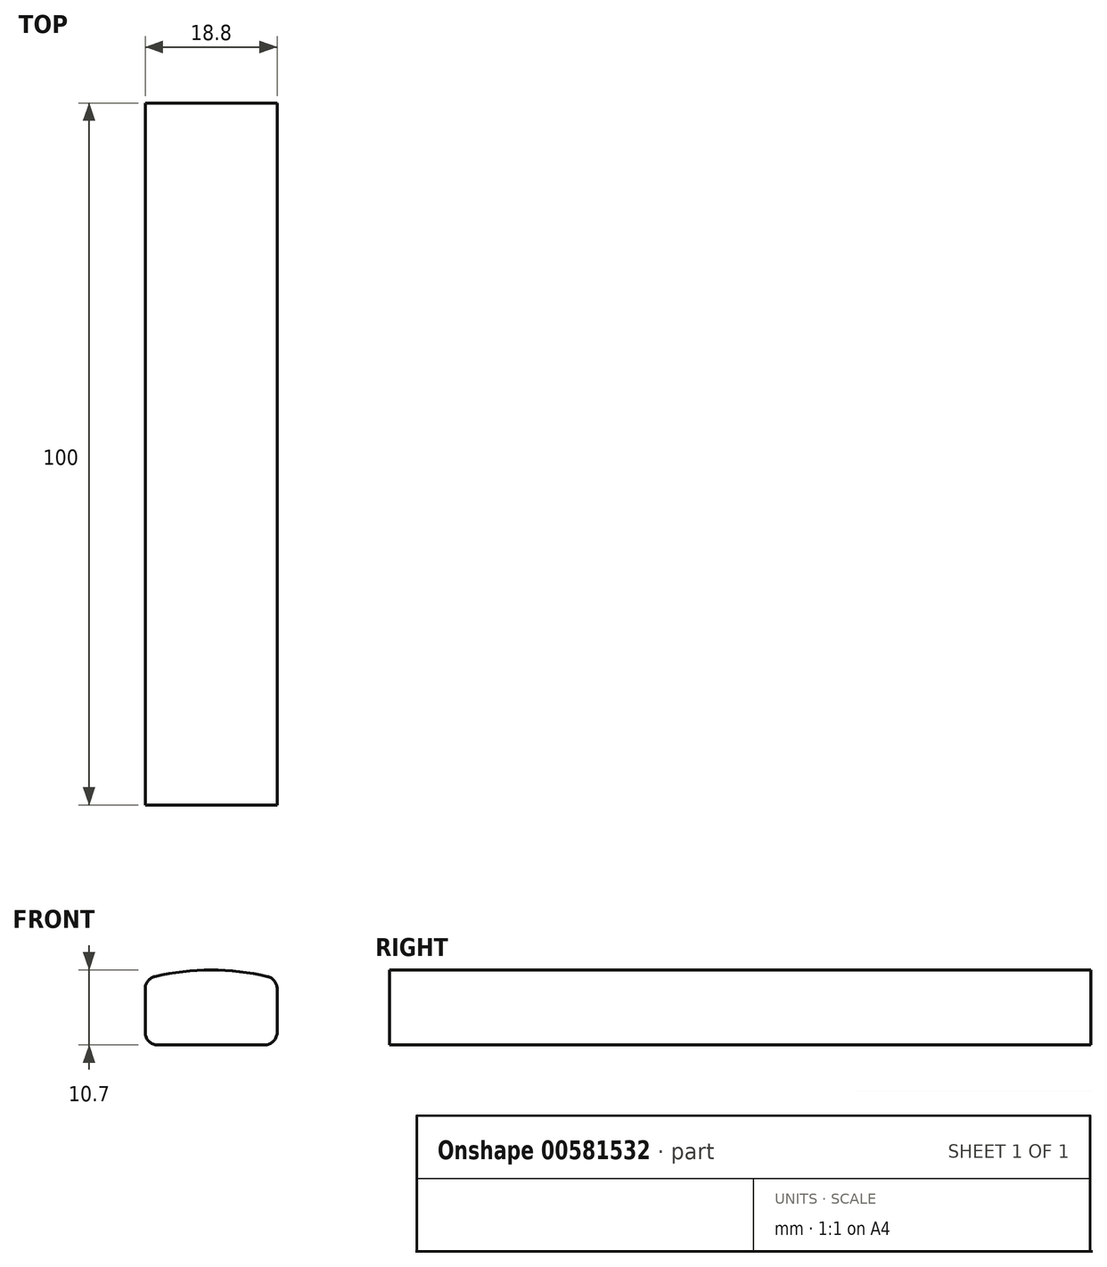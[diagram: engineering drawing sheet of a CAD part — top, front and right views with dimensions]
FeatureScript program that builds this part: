
annotation { "Feature Type Name" : "Feature", "Feature Type Description" : "" }
export const myFeature = defineFeature(function(context is Context, id is Id, definition is map)
    precondition{}
    {
        {
            var Q0;
            Q0=qCreatedBy(makeId("Front.planeOp"),FACE);
            var sketch = newSketch(context, id + "F0", { "sketchPlane" : qUnion([Q0])});
            skLineSegment(sketch, "E0.top", {"start": v(-7.6, -4.7) * mm, "end": v(7.6, -4.7) * mm});
            skLineSegment(sketch, "E0.left", {"start": v(-9.4, 3.3) * mm, "end": v(-9.4, -2.9) * mm});
            skLineSegment(sketch, "E0.right", {"start": v(9.4, 3.3) * mm, "end": v(9.4, -2.9) * mm});
            skPoint(sketch, "E0.middle", {"position": v(0, 0) * mm});
            skArc(sketch, "E1", {"start": v(-8.02, 5.06) * mm, "mid": v(0, 6) * mm, "end": v(8.02, 5.06) * mm});
            skPoint(sketch, "E2", {"position": v(0, 6) * mm});
            skPoint(sketch, "E3", {"position": v(0, -4.7) * mm});
            skPoint(sketch, "E4.visualSharp", {"position": v(-9.4, 4.7) * mm});
            skArc(sketch, "E4.filletArc", {"start": v(-8.02, 5.06) * mm, "mid": v(-9.01, 4.42) * mm, "end": v(-9.4, 3.3) * mm});
            skPoint(sketch, "E5.visualSharp", {"position": v(9.4, 4.7) * mm});
            skArc(sketch, "E5.filletArc", {"start": v(9.4, 3.3) * mm, "mid": v(9.01, 4.42) * mm, "end": v(8.02, 5.06) * mm});
            skPoint(sketch, "E6.visualSharp", {"position": v(-9.4, -4.7) * mm});
            skArc(sketch, "E6.filletArc", {"start": v(-9.4, -2.9) * mm, "mid": v(-8.87, -4.17) * mm, "end": v(-7.6, -4.7) * mm});
            skPoint(sketch, "E7.visualSharp", {"position": v(9.4, -4.7) * mm});
            skArc(sketch, "E7.filletArc", {"start": v(7.6, -4.7) * mm, "mid": v(8.87, -4.17) * mm, "end": v(9.4, -2.9) * mm});
            skSolve(sketch);
        }
        {
            var Q0;
            Q0=qSketchRegion(id+"F0",true);
            extrude(context, id + "F1", {"entities" : qUnion([Q0]), "depth" : 100 * mm});
        }
    });
